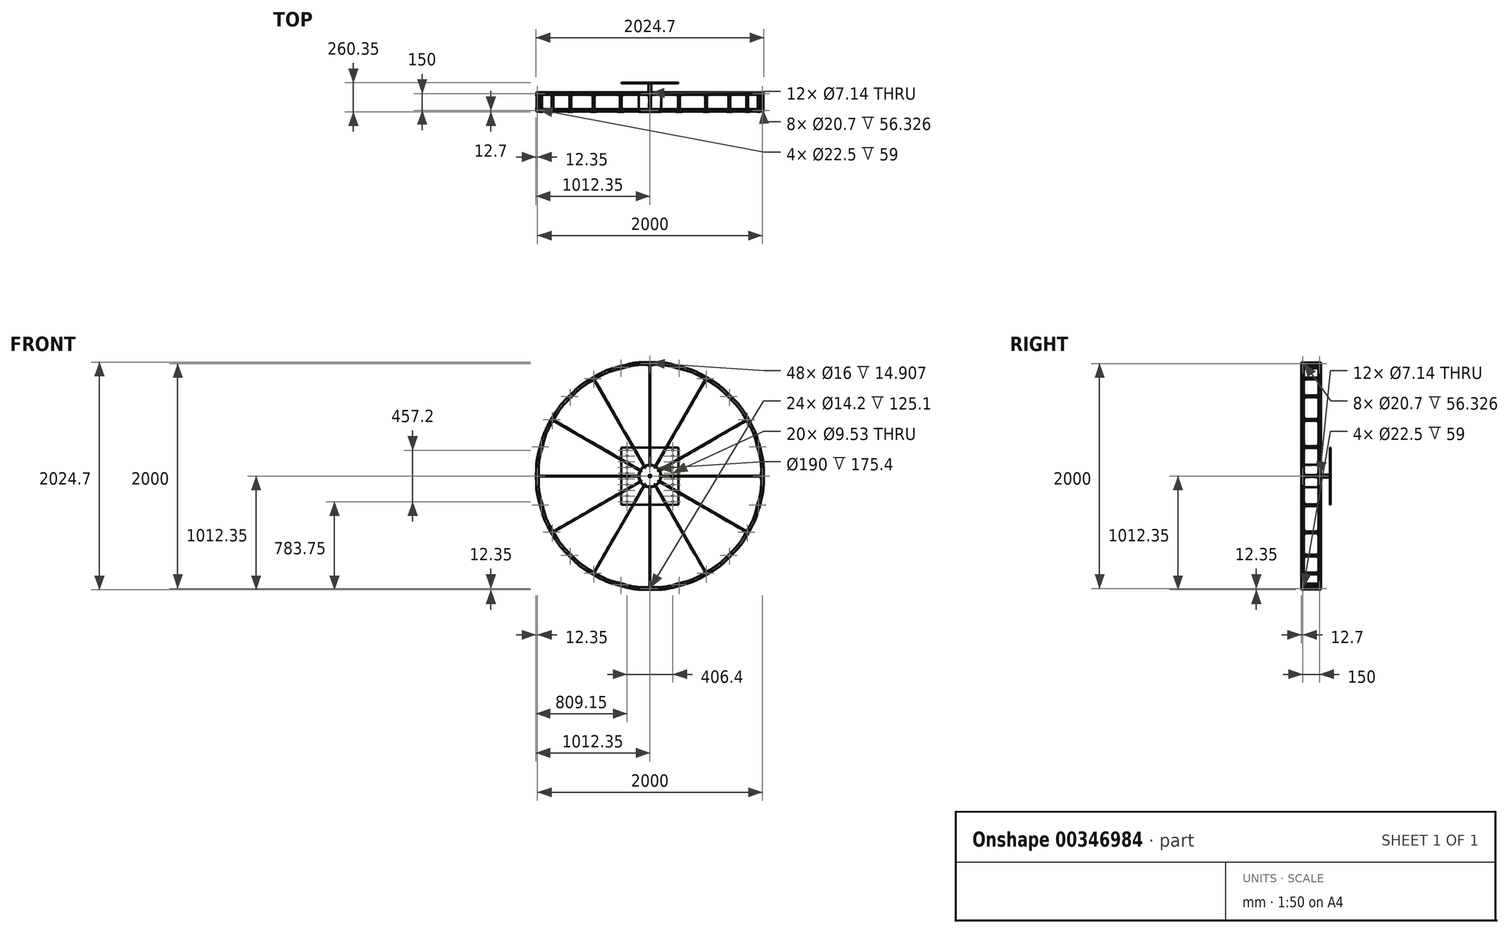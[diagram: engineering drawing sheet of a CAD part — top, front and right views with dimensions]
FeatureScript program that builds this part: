
annotation { "Feature Type Name" : "Feature", "Feature Type Description" : "" }
export const myFeature = defineFeature(function(context is Context, id is Id, definition is map)
    precondition{}
    {
        {
            assignVariable(context, id + "F0", {"name" : "spacing", "anyValue" : 150});
        }
        {
            assignVariable(context, id + "F1", {"name" : "spoke_length", "anyValue" : 914.4 * mm});
        }
        {
            assignVariable(context, id + "F2", {"name" : "Diameter", "anyValue" : 2000});
        }
        {
            assignVariable(context, id + "F3", {"name" : "Segments", "anyValue" : 24});
        }
        {
            assignVariable(context, id + "F4", {"name" : "spoke_count", "anyValue" : 12});
        }
        {
            var Q0;
            Q0=qCreatedBy(makeId("Right.planeOp"),FACE);
            var sketch = newSketch(context, id + "F5", { "sketchPlane" : qUnion([Q0])});
            skLineSegment(sketch, "E0", {"start": v(0, 0) * mm, "end": v(99.02, 0) * mm, "construction": true});
            skSolve(sketch);
        }
        {
            var Q0;
            Q0=qCreatedBy(makeId("Front.planeOp"),FACE);
            var sketch = newSketch(context, id + "F6", { "sketchPlane" : qUnion([Q0])});
            skCircle(sketch, "E1", {"center": v(0, 0) * mm, "radius": 1000 * mm, "construction": true});
            skLineSegment(sketch, "E2", {"start": v(0, 0) * mm, "end": v(0, 1000) * mm, "construction": true});
            skLineSegment(sketch, "E3", {"start": v(0, 0) * mm, "end": v(258.82, 965.93) * mm, "construction": true});
            skSolve(sketch);
        }
        {
            var Q0;
            Q0=qCreatedBy(makeId("Right.planeOp"),FACE);
            var sketch = newSketch(context, id + "F7", { "sketchPlane" : qUnion([Q0])});
            skCircle(sketch, "E4", {"center": v(0, 1000) * mm, "radius": 12.35 * mm});
            skCircle(sketch, "E5", {"center": v(0, 1000) * mm, "radius": 11.25 * mm});
            skSolve(sketch);
        }
        {
            var Q0;
            Q0=qCreatedBy(makeId("Front.planeOp"),FACE);
            var sketch = newSketch(context, id + "F8", { "sketchPlane" : qUnion([Q0])});
            skCircle(sketch, "E6", {"center": v(0, 1000) * mm, "radius": 9.1 * mm});
            skCircle(sketch, "E7", {"center": v(0, 1000) * mm, "radius": 8 * mm});
            skSolve(sketch);
        }
        {
            var Q0;
            Q0=qCreatedBy(makeId("Top.planeOp"),FACE);
            cPlane(context, id + "F9", {"entities" : qUnion([Q0]), "cplaneType" : CPlaneType.OFFSET, "offset" : (getVariable(context, 'Diameter') / 2) * mm, "width" : 150 * mm, "height" : 150 * mm});
        }
        {
            var Q0;
            Q0 = qSketchRegion(id + "F7", true);
            var Q1;
            Q1=sQuery(id+"F7.wireOp",EDGE,"E4");
            extrude(context, id + "F10", {"entities" : qUnion([Q0]), "surfaceEntities" : qUnion([Q1]), "depth" : (59 / 2) * mm, "hasSecondDirection" : true, "secondDirectionOppositeDirection" : true, "secondDirectionDepth" : (59 / 2) * mm});
        }
        {
            var Q0;
            Q0 = qSketchRegion(id + "F8", true);
            var Q1;
            Q1=sQuery(id+"F8.wireOp",EDGE,"E6");
            extrude(context, id + "F11", {"entities" : qUnion([Q0]), "operationType" : NewBodyOperationType.ADD, "surfaceEntities" : qUnion([Q1]), "oppositeDirection" : true, "depth" : 24.65 * mm});
        }
        {
            var Q0;
            Q0=makeQuery(id+"F7.imprint","IMPRINT",FACE,{"disambiguationData":[TD([[makeQuery(id+"F7.imprint","IMPRINT",EDGE,{"derivedFrom":sQuery(id+"F7.wireOp",EDGE,"E5")}),1.0]])]});
            extrude(context, id + "F12", {"entities" : qUnion([Q0]), "operationType" : NewBodyOperationType.REMOVE, "endBound" : BoundingType.THROUGH_ALL, "oppositeDirection" : true, "depth" : 25 * mm, "hasSecondDirection" : true, "secondDirectionBound" : SecondDirectionBoundingType.THROUGH_ALL, "secondDirectionOppositeDirection" : false, "secondDirectionDepth" : 25 * mm});
        }
        {
            var Q0;
            Q0=makeQuery(id+"F8.imprint","IMPRINT",FACE,{"disambiguationData":[TD([[makeQuery(id+"F8.imprint","IMPRINT",EDGE,{"derivedFrom":sQuery(id+"F8.wireOp",EDGE,"E7")}),1.0]])]});
            var Q1;
            Q1=sQuery(id+"F8.wireOp",EDGE,"E7");
            extrude(context, id + "F13", {"entities" : qUnion([Q0]), "operationType" : NewBodyOperationType.REMOVE, "surfaceEntities" : qUnion([Q1]), "endBound" : BoundingType.THROUGH_ALL, "oppositeDirection" : true, "depth" : 25 * mm});
        }
        {
            var Q0;
            {var subQ0=sQuery(id+"F8.wireOp",EDGE,"E7");var subQ1=sQuery(id+"F7.wireOp",EDGE,"E5");var subQ3=makeQuery(id+"F10.opExtrude","SWEPT_FACE",FACE,{"disambiguationData":[OSD([subQ1])]});Q0=makeQuery(id+"F13.boolean.opBoolean","INTERSECT",EDGE,{"derivedFrom":[makeQuery(id+"F12.boolean.opBoolean","MERGE",FACE,{"derivedFrom":[makeQuery(id+"F11.boolean.opBoolean","SPLIT",FACE,{"disambiguationData":[TD([makeQuery(id+"F11.opExtrude","SWEPT_FACE",FACE,{"disambiguationData":[OSD([subQ0])]})])],"derivedFrom":subQ3}),makeQuery(id+"F11.boolean.opBoolean","SPLIT",FACE,{"disambiguationData":[TD([makeQuery(id+"F11.opExtrude","SWEPT_FACE",FACE,{"disambiguationData":[OSD([sQuery(id+"F8.wireOp",EDGE,"E6")])]})])],"derivedFrom":subQ3}),makeQuery(id+"F12.opExtrude","SWEPT_FACE",FACE,{"disambiguationData":[OSD([subQ1])]})]}),makeQuery(id+"F13.opExtrude","SWEPT_FACE",FACE,{"disambiguationData":[OSD([subQ0])]})]});}
            var Q1;
            Q1=makeQuery(id+"F11.boolean.opBoolean","INTERSECT",EDGE,{"derivedFrom":[makeQuery(id+"F10.opExtrude","SWEPT_FACE",FACE,{"disambiguationData":[OSD([sQuery(id+"F7.wireOp",EDGE,"E4")])]}),makeQuery(id+"F11.opExtrude","SWEPT_FACE",FACE,{"disambiguationData":[OSD([sQuery(id+"F8.wireOp",EDGE,"E6")])]})]});
            fillet(context, id + "F14", {"entities" : qUnion([Q0, Q1]), "radius" : 5 * mm, "tangentPropagation" : true, "allowEdgeOverflow" : false});
        }
        {
            var Q0;
            Q0=qCreatedBy(id+"F9.planeOp",FACE);
            var sketch = newSketch(context, id + "F15", { "sketchPlane" : qUnion([Q0])});
            skCircle(sketch, "E8", {"center": v(0, 0) * mm, "radius": 3.57 * mm});
            skCircle(sketch, "E9", {"center": v(0, 0) * mm, "radius": 8 * mm});
            skSolve(sketch);
        }
        {
            var Q0;
            Q0=makeQuery(id+"F15.imprint","IMPRINT",FACE,{"disambiguationData":[TD([[makeQuery(id+"F15.imprint","IMPRINT",EDGE,{"derivedFrom":sQuery(id+"F15.wireOp",EDGE,"E8")}),1.0]])]});
            extrude(context, id + "F16", {"entities" : qUnion([Q0]), "operationType" : NewBodyOperationType.REMOVE, "endBound" : BoundingType.THROUGH_ALL, "oppositeDirection" : true, "depth" : 25 * mm});
        }
        {
            var Q0;
            Q0=qCreatedBy(makeId("Front.planeOp"),FACE);
            var sketch = newSketch(context, id + "F17", { "sketchPlane" : qUnion([Q0])});
            skLineSegment(sketch, "E10", {"start": v(0, 1000) * mm, "end": v(9.5, 1000) * mm, "construction": true});
            skLineSegment(sketch, "E11", {"start": v(258.82, 965.93) * mm, "end": v(249.64, 968.38) * mm, "construction": true});
            skLineSegment(sketch, "E12", {"start": v(9.5, 1000) * mm, "end": v(65.83, 1000) * mm});
            skLineSegment(sketch, "E13", {"start": v(195.24, 982.96) * mm, "end": v(249.64, 968.38) * mm});
            skPoint(sketch, "E14.visualSharp", {"position": v(131.65, 1000) * mm});
            skArc(sketch, "E14.filletArc", {"start": v(195.24, 982.96) * mm, "mid": v(131.09, 995.72) * mm, "end": v(65.83, 1000) * mm});
            skSolve(sketch);
        }
        {
            var Q0;
            Q0=sQuery(id+"F17.wireOp",VERTEX,"E10.end");
            var Q1;
            Q1=qCreatedBy(makeId("Right.planeOp"),FACE);
            cPlane(context, id + "F18", {"entities" : qUnion([Q0, Q1]), "cplaneType" : CPlaneType.PLANE_POINT, "offset" : 25 * mm, "width" : 150 * mm, "height" : 150 * mm});
        }
        {
            var Q0;
            Q0=qCreatedBy(id+"F18.planeOp",FACE);
            var sketch = newSketch(context, id + "F19", { "sketchPlane" : qUnion([Q0])});
            skCircle(sketch, "E15", {"center": v(0, 1000) * mm, "radius": 11.1 * mm});
            skCircle(sketch, "E16", {"center": v(0, 1000) * mm, "radius": 10.35 * mm});
            skSolve(sketch);
        }
        {
            var Q0;
            Q0=makeQuery(id+"F19.imprint","IMPRINT",FACE,{"disambiguationData":[TD([[makeQuery(id+"F19.imprint","IMPRINT",EDGE,{"derivedFrom":sQuery(id+"F19.wireOp",EDGE,"E15")}),1.0]])]});
            var Q1;
            Q1=sQuery(id+"F17.wireOp",EDGE,"E12");
            var Q2;
            Q2=sQuery(id+"F17.wireOp",EDGE,"E14.filletArc");
            var Q3;
            Q3=sQuery(id+"F17.wireOp",EDGE,"E13");
            sweep(context, id + "F20", {"profiles" : qUnion([Q0]), "path" : qUnion([Q1, Q2, Q3])});
        }
        {
            var Q0;
            Q0=qCreatedBy(makeId("Front.planeOp"),FACE);
            cPlane(context, id + "F21", {"entities" : qUnion([Q0]), "cplaneType" : CPlaneType.OFFSET, "offset" : 12.45 * mm, "oppositeDirection" : true, "width" : 150 * mm, "height" : 150 * mm});
        }
        {
            var Q0;
            Q0=qCreatedBy(id+"F21.planeOp",FACE);
            var sketch = newSketch(context, id + "F22", { "sketchPlane" : qUnion([Q0])});
            skCircle(sketch, "E17", {"center": v(0, 1000) * mm, "radius": 7.85 * mm});
            skCircle(sketch, "E18", {"center": v(0, 1000) * mm, "radius": 7.1 * mm});
            skSolve(sketch);
        }
        {
            var Q0;
            Q0=makeQuery(id+"F22.imprint","IMPRINT",FACE,{"disambiguationData":[TD([[makeQuery(id+"F22.imprint","IMPRINT",EDGE,{"derivedFrom":sQuery(id+"F22.wireOp",EDGE,"E17")}),1.0]])]});
            extrude(context, id + "F23", {"entities" : qUnion([Q0]), "operationType" : NewBodyOperationType.ADD, "oppositeDirection" : true, "depth" : (getVariable(context, 'spacing') - 24.9) * mm});
        }
        {
            var Q0;
            Q0=qCreatedBy(makeId("Front.planeOp"),FACE);
            cPlane(context, id + "F24", {"entities" : qUnion([Q0]), "cplaneType" : CPlaneType.OFFSET, "offset" : (getVariable(context, 'spacing') / 2) * mm, "oppositeDirection" : true, "width" : 150 * mm, "height" : 150 * mm});
        }
        {
            var Q0;
            Q0=qCreatedBy(id+"F9.planeOp",FACE);
            var sketch = newSketch(context, id + "F25", { "sketchPlane" : qUnion([Q0])});
            skCircle(sketch, "E19", {"center": v(0, 0) * mm, "radius": 3.18 * mm});
            skSolve(sketch);
        }
        {
            var Q0;
            Q0=makeQuery(id+"F25.imprint","IMPRINT",FACE,{"disambiguationData":[TD([[makeQuery(id+"F25.imprint","IMPRINT",EDGE,{"derivedFrom":sQuery(id+"F25.wireOp",EDGE,"E19")}),1.0]])]});
            extrude(context, id + "F26", {"entities" : qUnion([Q0]), "oppositeDirection" : true, "depth" : getVariable(context, 'spoke_length')});
        }
        {
            var Q0;
            Q0=makeQuery(id+"F26.opExtrude","CAP_FACE",FACE,{"disambiguationData":[OSD([sQuery(id+"F25.wireOp",EDGE,"E19")])],"isStart":false});
            var sketch = newSketch(context, id + "F27", { "sketchPlane" : qUnion([Q0])});
            skCircle(sketch, "E20.cCircle", {"center": v(0, 0) * mm, "radius": 5.56 * mm, "construction": true});
            skLineSegment(sketch, "E20.0", {"start": v(3.2, 5.56) * mm, "end": v(6.42, 0) * mm});
            skLineSegment(sketch, "E20.1", {"start": v(6.42, 0) * mm, "end": v(3.2, -5.56) * mm});
            skLineSegment(sketch, "E20.2", {"start": v(3.2, -5.56) * mm, "end": v(-3.2, -5.56) * mm});
            skLineSegment(sketch, "E20.3", {"start": v(-3.2, -5.56) * mm, "end": v(-6.42, 0) * mm});
            skLineSegment(sketch, "E20.4", {"start": v(-6.42, 0) * mm, "end": v(-3.2, 5.56) * mm});
            skLineSegment(sketch, "E20.5", {"start": v(-3.2, 5.56) * mm, "end": v(3.2, 5.56) * mm});
            skPoint(sketch, "E20.0.midPoint", {"position": v(4.81, 2.78) * mm});
            skCircle(sketch, "E21.0.0", {"center": v(0, 0) * mm, "radius": 3.18 * mm});
            skSolve(sketch);
        }
        {
            var Q0;
            Q0 = qSketchRegion(id + "F27", true);
            extrude(context, id + "F28", {"entities" : qUnion([Q0]), "oppositeDirection" : true, "depth" : 7 / 812.8 * mm});
        }
        {
            var Q0;
            Q0=makeQuery(id+"F10.opExtrude","SWEPT_BODY",BODY,{"disambiguationData":[OSD([sQuery(id+"F7.wireOp",EDGE,"E4"),sQuery(id+"F7.wireOp",EDGE,"E5")])]});
            var Q1;
            Q1=makeQuery(id+"F20.opSweep","SWEPT_BODY",BODY,{"disambiguationData":[OSD([sQuery(id+"F17.wireOp",EDGE,"E13"),sQuery(id+"F19.wireOp",EDGE,"E15"),sQuery(id+"F19.wireOp",EDGE,"E16")])]});
            var Q2;
            Q2=makeQuery(id+"F26.opExtrude","SWEPT_BODY",BODY,{"disambiguationData":[OSD([sQuery(id+"F25.wireOp",EDGE,"E19")])]});
            var Q3;
            Q3=makeQuery(id+"F28.opExtrude","SWEPT_BODY",BODY,{"disambiguationData":[OSD([sQuery(id+"F27.wireOp",EDGE,"E20.0"),sQuery(id+"F27.wireOp",EDGE,"E20.1"),sQuery(id+"F27.wireOp",EDGE,"E20.2"),sQuery(id+"F27.wireOp",EDGE,"E20.3"),sQuery(id+"F27.wireOp",EDGE,"E20.4"),sQuery(id+"F27.wireOp",EDGE,"E20.5"),sQuery(id+"F27.wireOp",EDGE,"E21.0.0")])]});
            var Q4;
            Q4=qCreatedBy(id+"F24.planeOp",FACE);
            mirror(context, id + "F29", {"entities" : qUnion([Q0, Q1, Q2, Q3]), "mirrorPlane" : qUnion([Q4])});
        }
        {
            var Q0;
            Q0=makeQuery(id+"F10.opExtrude","SWEPT_BODY",BODY,{"disambiguationData":[OSD([sQuery(id+"F7.wireOp",EDGE,"E4"),sQuery(id+"F7.wireOp",EDGE,"E5")])]});
            var Q1;
            Q1=makeQuery(id+"F23.opExtrude","SWEPT_BODY",BODY,{"disambiguationData":[OSD([sQuery(id+"F22.wireOp",EDGE,"E17"),sQuery(id+"F22.wireOp",EDGE,"E18")])]});
            var Q2;
            Q2=makeQuery(id+"F20.opSweep","SWEPT_BODY",BODY,{"disambiguationData":[OSD([sQuery(id+"F17.wireOp",EDGE,"E13"),sQuery(id+"F19.wireOp",EDGE,"E15"),sQuery(id+"F19.wireOp",EDGE,"E16")])]});
            var Q3;
            Q3=makeQuery(id+"F29.opPattern","COPY",BODY,{"derivedFrom":makeQuery(id+"F20.opSweep","SWEPT_BODY",BODY,{"disambiguationData":[OSD([sQuery(id+"F17.wireOp",EDGE,"E13"),sQuery(id+"F19.wireOp",EDGE,"E15"),sQuery(id+"F19.wireOp",EDGE,"E16")])]}),"instanceName":"1"});
            var Q4;
            Q4=makeQuery(id+"F29.opPattern","COPY",BODY,{"derivedFrom":makeQuery(id+"F10.opExtrude","SWEPT_BODY",BODY,{"disambiguationData":[OSD([sQuery(id+"F7.wireOp",EDGE,"E4"),sQuery(id+"F7.wireOp",EDGE,"E5")])]}),"instanceName":"1"});
            var Q5;
            Q5=sQuery(id+"F5.wireOp",EDGE,"E0");
            circularPattern(context, id + "F30", {"entities" : qUnion([Q0, Q1, Q2, Q3, Q4]), "axis" : qUnion([Q5]), "angle" : 360 * degree, "instanceCount" : getVariable(context, 'Segments'), "equalSpace" : true});
        }
        {
            var Q0;
            Q0=qCreatedBy(makeId("Front.planeOp"),FACE);
            var sketch = newSketch(context, id + "F31", { "sketchPlane" : qUnion([Q0])});
            skCircle(sketch, "E22", {"center": v(0, 0) * mm, "radius": 100 * mm});
            skLineSegment(sketch, "E23.1", {"start": v(-3.18, 85.6) * mm, "end": v(3.18, 85.6) * mm, "construction": true});
            skCircle(sketch, "E24.0", {"center": v(0, 0) * mm, "radius": 95 * mm});
            skSolve(sketch);
        }
        {
            var Q0;
            Q0 = qSketchRegion(id + "F31", true);
            extrude(context, id + "F32", {"entities" : qUnion([Q0]), "depth" : 12.7 * mm, "hasSecondDirection" : true, "secondDirectionOppositeDirection" : true, "secondDirectionDepth" : getVariable(context, 'spacing') * mm + 12.7 * mm});
        }
        {
            var Q0;
            Q0=qCreatedBy(makeId("Top.planeOp"),FACE);
            var sketch = newSketch(context, id + "F33", { "sketchPlane" : qUnion([Q0])});
            skCircle(sketch, "E25", {"center": v(0, 0) * mm, "radius": 3.57 * mm});
            skSolve(sketch);
        }
        {
            var Q0;
            Q0 = qSketchRegion(id + "F33", true);
            var Q1;
            Q1=makeQuery(id+"F32.opExtrude","SWEPT_FACE",FACE,{"disambiguationData":[OSD([sQuery(id+"F31.wireOp",EDGE,"E22")])]});
            extrude(context, id + "F34", {"entities" : qUnion([Q0]), "endBound" : BoundingType.UP_TO_SURFACE, "oppositeDirection" : true, "endBoundEntityFace" : qUnion([Q1]), "depth" : 25 * mm});
        }
        {
            var Q0;
            Q0=makeQuery(id+"F34.opExtrude","SWEPT_BODY",BODY,{"disambiguationData":[OSD([sQuery(id+"F33.wireOp",EDGE,"E25")])]});
            var Q1;
            Q1=qCreatedBy(id+"F24.planeOp",FACE);
            mirror(context, id + "F35", {"entities" : qUnion([Q0]), "mirrorPlane" : qUnion([Q1])});
        }
        {
            var Q0;
            Q0=makeQuery(id+"F34.opExtrude","SWEPT_BODY",BODY,{"disambiguationData":[OSD([sQuery(id+"F33.wireOp",EDGE,"E25")])]});
            var Q1;
            Q1=makeQuery(id+"F35.opPattern","COPY",BODY,{"derivedFrom":makeQuery(id+"F34.opExtrude","SWEPT_BODY",BODY,{"disambiguationData":[OSD([sQuery(id+"F33.wireOp",EDGE,"E25")])]}),"instanceName":"1"});
            var Q2;
            Q2=sQuery(id+"F5.wireOp",EDGE,"E0");
            circularPattern(context, id + "F36", {"operationType" : NewBodyOperationType.REMOVE, "entities" : qUnion([Q0, Q1]), "axis" : qUnion([Q2]), "angle" : 360 * degree, "instanceCount" : getVariable(context, 'spoke_count'), "equalSpace" : true});
        }
        {
            var Q0;
            Q0=qCreatedBy(makeId("Front.planeOp"),FACE);
            var sketch = newSketch(context, id + "F37", { "sketchPlane" : qUnion([Q0])});
            skCircle(sketch, "E26", {"center": v(0, 0) * mm, "radius": 12.7 * mm});
            skSolve(sketch);
        }
        {
            var Q0;
            Q0 = qSketchRegion(id + "F37", true);
            extrude(context, id + "F38", {"entities" : qUnion([Q0]), "depth" : 12.7 * mm, "hasSecondDirection" : true, "secondDirectionOppositeDirection" : true, "secondDirectionDepth" : 241.3 * mm});
        }
        {
            var Q0;
            Q0=makeQuery(id+"F38.opExtrude","CAP_FACE",FACE,{"disambiguationData":[OSD([sQuery(id+"F37.wireOp",EDGE,"E26")])],"isStart":true});
            var sketch = newSketch(context, id + "F39", { "sketchPlane" : qUnion([Q0])});
            skLineSegment(sketch, "E27.bottom", {"start": v(-254, 254) * mm, "end": v(254, 254) * mm});
            skLineSegment(sketch, "E27.top", {"start": v(-254, -254) * mm, "end": v(254, -254) * mm});
            skLineSegment(sketch, "E27.left", {"start": v(-254, 254) * mm, "end": v(-254, -254) * mm});
            skLineSegment(sketch, "E27.right", {"start": v(254, 254) * mm, "end": v(254, -254) * mm});
            skLineSegment(sketch, "E28", {"start": v(-254, 254) * mm, "end": v(254, -254) * mm, "construction": true});
            skCircle(sketch, "E29", {"center": v(203.2, -228.6) * mm, "radius": 4.76 * mm});
            skCircle(sketch, "E30.0.1.0", {"center": v(203.2, -177.8) * mm, "radius": 4.76 * mm});
            skCircle(sketch, "E30.0.2.0", {"center": v(203.2, -127) * mm, "radius": 4.76 * mm});
            skCircle(sketch, "E30.0.3.0", {"center": v(203.2, -76.2) * mm, "radius": 4.76 * mm});
            skCircle(sketch, "E30.0.4.0", {"center": v(203.2, -25.4) * mm, "radius": 4.76 * mm});
            skCircle(sketch, "E30.0.5.0", {"center": v(203.2, 25.4) * mm, "radius": 4.76 * mm});
            skCircle(sketch, "E30.0.6.0", {"center": v(203.2, 76.2) * mm, "radius": 4.76 * mm});
            skCircle(sketch, "E30.0.7.0", {"center": v(203.2, 127) * mm, "radius": 4.76 * mm});
            skCircle(sketch, "E30.0.8.0", {"center": v(203.2, 177.8) * mm, "radius": 4.76 * mm});
            skCircle(sketch, "E30.0.9.0", {"center": v(203.2, 228.6) * mm, "radius": 4.76 * mm});
            skCircle(sketch, "E30.1.0.0", {"center": v(-203.2, -228.6) * mm, "radius": 4.76 * mm});
            skCircle(sketch, "E30.1.1.0", {"center": v(-203.2, -177.8) * mm, "radius": 4.76 * mm});
            skCircle(sketch, "E30.1.2.0", {"center": v(-203.2, -127) * mm, "radius": 4.76 * mm});
            skCircle(sketch, "E30.1.3.0", {"center": v(-203.2, -76.2) * mm, "radius": 4.76 * mm});
            skCircle(sketch, "E30.1.4.0", {"center": v(-203.2, -25.4) * mm, "radius": 4.76 * mm});
            skCircle(sketch, "E30.1.5.0", {"center": v(-203.2, 25.4) * mm, "radius": 4.76 * mm});
            skCircle(sketch, "E30.1.6.0", {"center": v(-203.2, 76.2) * mm, "radius": 4.76 * mm});
            skCircle(sketch, "E30.1.7.0", {"center": v(-203.2, 127) * mm, "radius": 4.76 * mm});
            skCircle(sketch, "E30.1.8.0", {"center": v(-203.2, 177.8) * mm, "radius": 4.76 * mm});
            skCircle(sketch, "E30.1.9.0", {"center": v(-203.2, 228.6) * mm, "radius": 4.76 * mm});
            skLineSegment(sketch, "E30.direction1", {"start": v(203.2, -228.6) * mm, "end": v(-203.2, -228.6) * mm, "construction": true});
            skLineSegment(sketch, "E30.direction2", {"start": v(203.2, -228.6) * mm, "end": v(203.2, -177.8) * mm, "construction": true});
            skSolve(sketch);
        }
        {
            var Q0;
            Q0 = qSketchRegion(id + "F39", true);
            extrude(context, id + "F40", {"entities" : qUnion([Q0]), "operationType" : NewBodyOperationType.ADD, "depth" : 6.35 * mm});
        }
        {
            var Q0;
            Q0=qCreatedBy(makeId("Front.planeOp"),FACE);
            cPlane(context, id + "F41", {"entities" : qUnion([Q0]), "cplaneType" : CPlaneType.OFFSET, "offset" : 1 / 50.8 * mm, "oppositeDirection" : true, "width" : 150 * mm, "height" : 150 * mm});
        }
        {
            var Q0;
            Q0=qCreatedBy(id+"F41.planeOp",FACE);
            var sketch = newSketch(context, id + "F42", { "sketchPlane" : qUnion([Q0])});
            skCircle(sketch, "E31.0.0", {"center": v(0, 0) * mm, "radius": 12.7 * mm, "construction": true});
            skCircle(sketch, "E32", {"center": v(0, 0) * mm, "radius": 95 * mm});
            skCircle(sketch, "E33", {"center": v(0, 0) * mm, "radius": 19.05 * mm});
            skSolve(sketch);
        }
        {
            var Q0;
            Q0=makeQuery(id+"F28.opExtrude","SWEPT_BODY",BODY,{"disambiguationData":[OSD([sQuery(id+"F27.wireOp",EDGE,"E20.0"),sQuery(id+"F27.wireOp",EDGE,"E20.1"),sQuery(id+"F27.wireOp",EDGE,"E20.2"),sQuery(id+"F27.wireOp",EDGE,"E20.3"),sQuery(id+"F27.wireOp",EDGE,"E20.4"),sQuery(id+"F27.wireOp",EDGE,"E20.5"),sQuery(id+"F27.wireOp",EDGE,"E21.0.0")])]});
            var Q1;
            Q1=makeQuery(id+"F26.opExtrude","SWEPT_BODY",BODY,{"disambiguationData":[OSD([sQuery(id+"F25.wireOp",EDGE,"E19")])]});
            var Q2;
            Q2=makeQuery(id+"F29.opPattern","COPY",BODY,{"derivedFrom":makeQuery(id+"F26.opExtrude","SWEPT_BODY",BODY,{"disambiguationData":[OSD([sQuery(id+"F25.wireOp",EDGE,"E19")])]}),"instanceName":"1"});
            var Q3;
            Q3=makeQuery(id+"F29.opPattern","COPY",BODY,{"derivedFrom":makeQuery(id+"F28.opExtrude","SWEPT_BODY",BODY,{"disambiguationData":[OSD([sQuery(id+"F27.wireOp",EDGE,"E20.0"),sQuery(id+"F27.wireOp",EDGE,"E20.1"),sQuery(id+"F27.wireOp",EDGE,"E20.2"),sQuery(id+"F27.wireOp",EDGE,"E20.3"),sQuery(id+"F27.wireOp",EDGE,"E20.4"),sQuery(id+"F27.wireOp",EDGE,"E20.5"),sQuery(id+"F27.wireOp",EDGE,"E21.0.0")])]}),"instanceName":"1"});
            var Q4;
            Q4=sQuery(id+"F5.wireOp",EDGE,"E0");
            circularPattern(context, id + "F43", {"entities" : qUnion([Q0, Q1, Q2, Q3]), "axis" : qUnion([Q4]), "angle" : 360 * degree, "instanceCount" : getVariable(context, 'spoke_count'), "equalSpace" : true});
        }
    });
